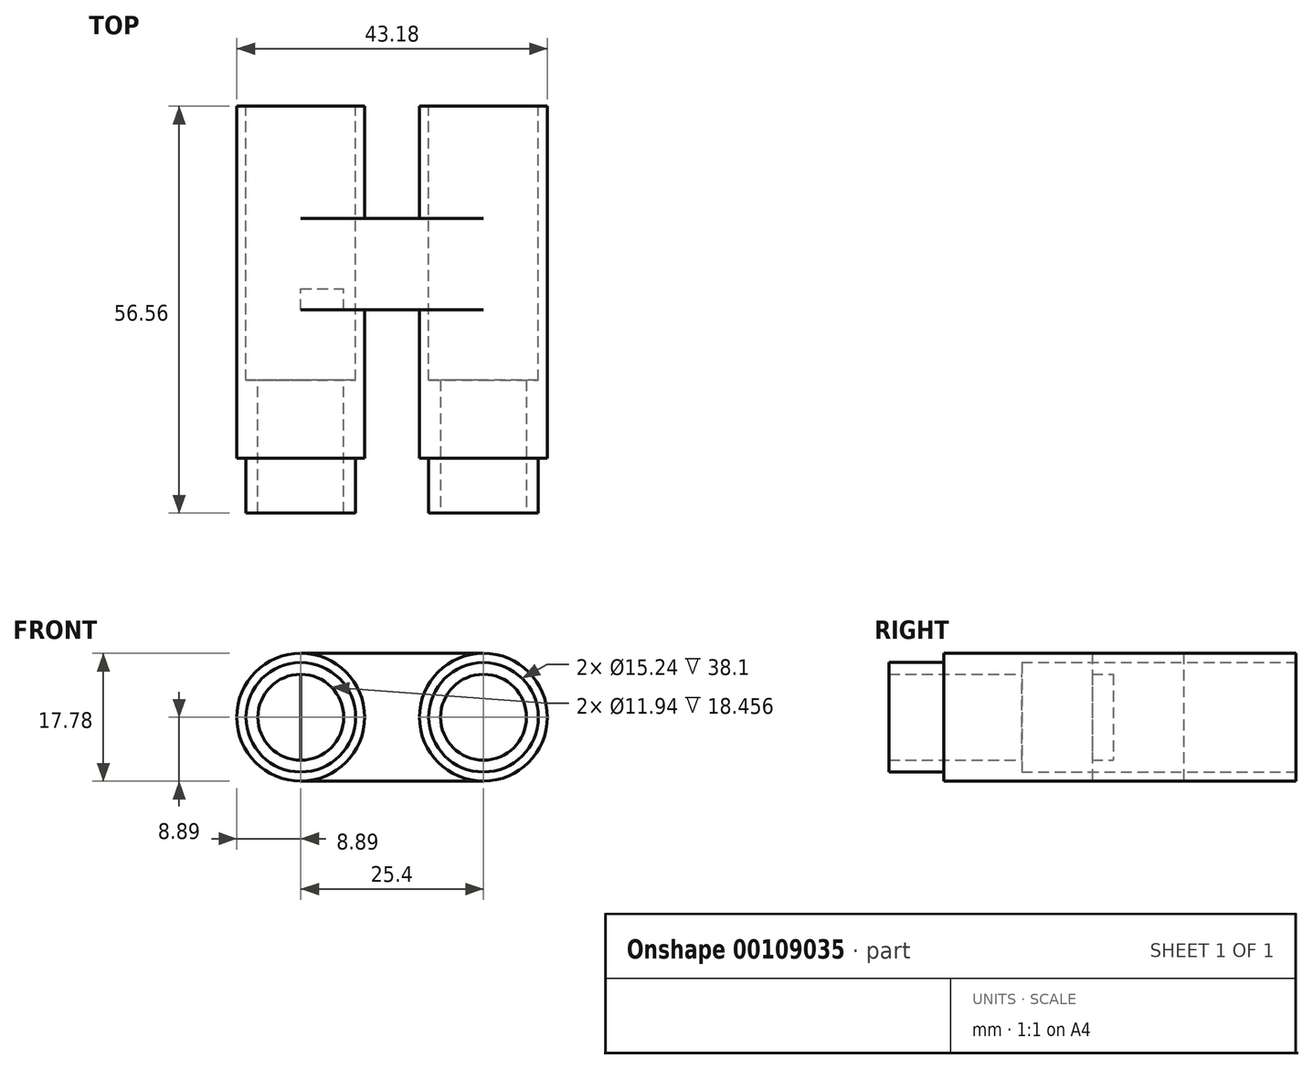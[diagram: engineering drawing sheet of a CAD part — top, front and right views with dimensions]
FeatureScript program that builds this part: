
annotation { "Feature Type Name" : "Feature", "Feature Type Description" : "" }
export const myFeature = defineFeature(function(context is Context, id is Id, definition is map)
    precondition{}
    {
        {
            var Q0;
            Q0=qCreatedBy(makeId("Top.planeOp"),FACE);
            var sketch = newSketch(context, id + "F0", { "sketchPlane" : qUnion([Q0])});
            skLineSegment(sketch, "E0", {"start": v(0, 0) * mm, "end": v(25.4, 0) * mm});
            skLineSegment(sketch, "E1", {"start": v(0, 0) * mm, "end": v(0, 124.47) * mm});
            skLineSegment(sketch, "E2", {"start": v(25.4, 0) * mm, "end": v(25.4, 124.47) * mm});
            skArc(sketch, "E3", {"start": v(0, 124.47) * mm, "mid": v(12.7, 137.17) * mm, "end": v(25.4, 124.47) * mm});
            skLineSegment(sketch, "E4", {"start": v(12.7, 137.17) * mm, "end": v(12.7, 56.56) * mm});
            skLineSegment(sketch, "E5", {"start": v(12.7, 56.56) * mm, "end": v(45.11, 56.56) * mm});
            skLineSegment(sketch, "E6", {"start": v(12.7, 56.56) * mm, "end": v(-27.35, 56.56) * mm});
            skLineSegment(sketch, "E7", {"start": v(-27.35, 56.56) * mm, "end": v(-27.35, 146.64) * mm});
            skLineSegment(sketch, "E8", {"start": v(-27.35, 146.64) * mm, "end": v(45.11, 146.64) * mm});
            skLineSegment(sketch, "E9", {"start": v(45.11, 56.56) * mm, "end": v(45.11, 146.64) * mm});
            skLineSegment(sketch, "E10", {"start": v(0, 40.94) * mm, "end": v(25.4, 40.94) * mm});
            skLineSegment(sketch, "E11", {"start": v(0, 28.24) * mm, "end": v(25.4, 28.24) * mm});
            skSolve(sketch);
        }
        {
            var Q0;
            Q0=qCreatedBy(makeId("Front.planeOp"),FACE);
            var sketch = newSketch(context, id + "F1", { "sketchPlane" : qUnion([Q0])});
            skCircle(sketch, "E12", {"center": v(0, 0) * mm, "radius": 5.97 * mm});
            skCircle(sketch, "E13", {"center": v(0, 0) * mm, "radius": 8.9 * mm});
            skSolve(sketch);
        }
        {
            var Q0;
            Q0=makeQuery(id+"F1.imprint","IMPRINT",FACE,{"disambiguationData":[TD([[makeQuery(id+"F1.imprint","IMPRINT",EDGE,{"derivedFrom":sQuery(id+"F1.wireOp",EDGE,"E12")}),-1.0]])]});
            var Q1;
            Q1=sQuery(id+"F0.wireOp",EDGE,"E1");
            var Q2;
            Q2=sQuery(id+"F0.wireOp",EDGE,"E3");
            var Q3;
            Q3=sQuery(id+"F0.wireOp",EDGE,"E2");
            sweep(context, id + "F2", {"profiles" : qUnion([Q0]), "path" : qUnion([Q1, Q2, Q3])});
        }
        {
            var Q0;
            Q0=makeQuery(id+"F2.opSweep","CAP_FACE",FACE,{"disambiguationData":[OSD([sQuery(id+"F0.wireOp",VERTEX,"E1.start"),sQuery(id+"F1.wireOp",EDGE,"E12"),sQuery(id+"F1.wireOp",EDGE,"E13")])],"isStart":true});
            var sketch = newSketch(context, id + "F3", { "sketchPlane" : qUnion([Q0])});
            skCircle(sketch, "E14", {"center": v(0, 0) * mm, "radius": 7.62 * mm});
            skCircle(sketch, "E15", {"center": v(25.4, 0) * mm, "radius": 7.62 * mm});
            skLineSegment(sketch, "E16", {"start": v(0, 0) * mm, "end": v(25.4, 0) * mm});
            skCircle(sketch, "E17", {"center": v(25.4, 0) * mm, "radius": 8.9 * mm});
            skSolve(sketch);
        }
        {
            var Q0;
            Q0=makeQuery(id+"F3.imprint","IMPRINT",FACE,{"disambiguationData":[TD([[makeQuery(id+"F3.imprint","IMPRINT",EDGE,{"derivedFrom":sQuery(id+"F3.wireOp",EDGE,"E14")}),-1.0]])]});
            var Q1;
            Q1=makeQuery(id+"F3.imprint","IMPRINT",FACE,{"disambiguationData":[TD([[makeQuery(id+"F3.imprint","IMPRINT",EDGE,{"derivedFrom":sQuery(id+"F3.wireOp",EDGE,"E15")}),-1.0]])]});
            extrude(context, id + "F4", {"entities" : qUnion([Q0, Q1]), "operationType" : NewBodyOperationType.REMOVE, "oppositeDirection" : true, "depth" : 7.62 * mm});
        }
        {
            var Q0;
            {var subQ6=sQuery(id+"F0.wireOp",EDGE,"E7");Q0=makeQuery(id+"F0.imprint","IMPRINT",FACE,{"disambiguationData":[TD([[makeQuery(id+"F0.imprint","IMPRINT",EDGE,{"derivedFrom":subQ6}),-1.0]])]});}
            var Q1;
            {var subQ5=sQuery(id+"F0.wireOp",EDGE,"E4");Q1=makeQuery(id+"F0.imprint","IMPRINT",FACE,{"disambiguationData":[TD([[makeQuery(id+"F0.imprint","IMPRINT",EDGE,{"derivedFrom":subQ5}),-1.0]])]});}
            var Q2;
            {var subQ5=sQuery(id+"F0.wireOp",EDGE,"E4");Q2=makeQuery(id+"F0.imprint","IMPRINT",FACE,{"disambiguationData":[TD([[makeQuery(id+"F0.imprint","IMPRINT",EDGE,{"derivedFrom":subQ5}),1.0]])]});}
            extrude(context, id + "F5", {"entities" : qUnion([Q0, Q1, Q2]), "operationType" : NewBodyOperationType.REMOVE, "oppositeDirection" : true, "depth" : 25.4 * mm, "hasSecondDirection" : true, "secondDirectionOppositeDirection" : false, "secondDirectionDepth" : 25.4 * mm});
        }
        {
            var Q0;
            Q0=makeQuery(id+"F5.boolean.opBoolean","COPY",FACE,{"disambiguationData":[OD(1.0)],"derivedFrom":makeQuery(id+"F5.opExtrude","SWEPT_FACE",FACE,{"disambiguationData":[OSD([sQuery(id+"F0.wireOp",EDGE,"E5"),sQuery(id+"F0.wireOp",EDGE,"E6")])]})});
            var sketch = newSketch(context, id + "F6", { "sketchPlane" : qUnion([Q0])});
            skCircle(sketch, "E18", {"center": v(-25.4, 0) * mm, "radius": 7.62 * mm});
            skSolve(sketch);
        }
        {
            var Q0;
            Q0=makeQuery(id+"F5.boolean.opBoolean","COPY",FACE,{"disambiguationData":[OD(0.0)],"derivedFrom":makeQuery(id+"F5.opExtrude","SWEPT_FACE",FACE,{"disambiguationData":[OSD([sQuery(id+"F0.wireOp",EDGE,"E5"),sQuery(id+"F0.wireOp",EDGE,"E6")])]})});
            var sketch = newSketch(context, id + "F7", { "sketchPlane" : qUnion([Q0])});
            skCircle(sketch, "E19", {"center": v(0, 0) * mm, "radius": 7.62 * mm});
            skSolve(sketch);
        }
        {
            var Q0;
            Q0=makeQuery(id+"F6.imprint","IMPRINT",FACE,{"disambiguationData":[TD([[makeQuery(id+"F6.imprint","IMPRINT",EDGE,{"derivedFrom":sQuery(id+"F6.wireOp",EDGE,"E18")}),1.0]])]});
            var Q1;
            Q1=makeQuery(id+"F7.imprint","IMPRINT",FACE,{"disambiguationData":[TD([[makeQuery(id+"F7.imprint","IMPRINT",EDGE,{"derivedFrom":sQuery(id+"F7.wireOp",EDGE,"E19")}),1.0]])]});
            extrude(context, id + "F8", {"entities" : qUnion([Q0, Q1]), "operationType" : NewBodyOperationType.REMOVE, "oppositeDirection" : true, "depth" : 38.1 * mm});
        }
        {
            var Q0;
            {var subQ0=sQuery(id+"F0.wireOp",EDGE,"E10");Q0=makeQuery(id+"F0.imprint","IMPRINT",FACE,{"disambiguationData":[TD([[makeQuery(id+"F0.imprint","IMPRINT",EDGE,{"derivedFrom":subQ0}),-1.0]])]});}
            extrude(context, id + "F9", {"entities" : qUnion([Q0]), "operationType" : NewBodyOperationType.ADD, "depth" : 8.9 * mm, "hasSecondDirection" : true, "secondDirectionOppositeDirection" : true, "secondDirectionDepth" : 8.9 * mm});
        }
        {
            var Q0;
            Q0 = qSketchRegion(id + "F7", true);
            var Q1;
            Q1 = qSketchRegion(id + "F6", true);
            extrude(context, id + "F10", {"entities" : qUnion([Q0, Q1]), "operationType" : NewBodyOperationType.REMOVE, "oppositeDirection" : true, "depth" : 25.4 * mm});
        }
        {
            var Q0;
            Q0=makeQuery(id+"F7.imprint","IMPRINT",FACE,{"disambiguationData":[TD([[makeQuery(id+"F7.imprint","IMPRINT",EDGE,{"derivedFrom":sQuery(id+"F7.wireOp",EDGE,"E19")}),1.0]])]});
            var Q1;
            Q1=makeQuery(id+"F7.imprint","IMPRINT",FACE,{"disambiguationData":[TD([[makeQuery(id+"F7.imprint","IMPRINT",EDGE,{"derivedFrom":makeQuery(id+"F5.boolean.opBoolean","INTERSECT",EDGE,{"derivedFrom":[makeQuery(id+"F2.opSweep","SWEPT_FACE",FACE,{"disambiguationData":[OSD([sQuery(id+"F0.wireOp",EDGE,"E1"),sQuery(id+"F1.wireOp",EDGE,"E12")])]}),makeQuery(id+"F5.opExtrude","SWEPT_FACE",FACE,{"disambiguationData":[OSD([sQuery(id+"F0.wireOp",EDGE,"E5"),sQuery(id+"F0.wireOp",EDGE,"E6")])]})]})}),1.0]])]});
            var Q2;
            Q2=makeQuery(id+"F6.imprint","IMPRINT",FACE,{"disambiguationData":[TD([[makeQuery(id+"F6.imprint","IMPRINT",EDGE,{"derivedFrom":makeQuery(id+"F5.boolean.opBoolean","INTERSECT",EDGE,{"derivedFrom":[makeQuery(id+"F2.opSweep","SWEPT_FACE",FACE,{"disambiguationData":[OSD([sQuery(id+"F0.wireOp",EDGE,"E2"),sQuery(id+"F1.wireOp",EDGE,"E12")])]}),makeQuery(id+"F5.opExtrude","SWEPT_FACE",FACE,{"disambiguationData":[OSD([sQuery(id+"F0.wireOp",EDGE,"E5"),sQuery(id+"F0.wireOp",EDGE,"E6")])]})]})}),1.0]])]});
            var Q3;
            Q3=makeQuery(id+"F6.imprint","IMPRINT",FACE,{"disambiguationData":[TD([[makeQuery(id+"F6.imprint","IMPRINT",EDGE,{"derivedFrom":sQuery(id+"F6.wireOp",EDGE,"E18")}),1.0]])]});
            extrude(context, id + "F11", {"entities" : qUnion([Q0, Q1, Q2, Q3]), "operationType" : NewBodyOperationType.REMOVE, "oppositeDirection" : true, "depth" : 38.1 * mm});
        }
    });
